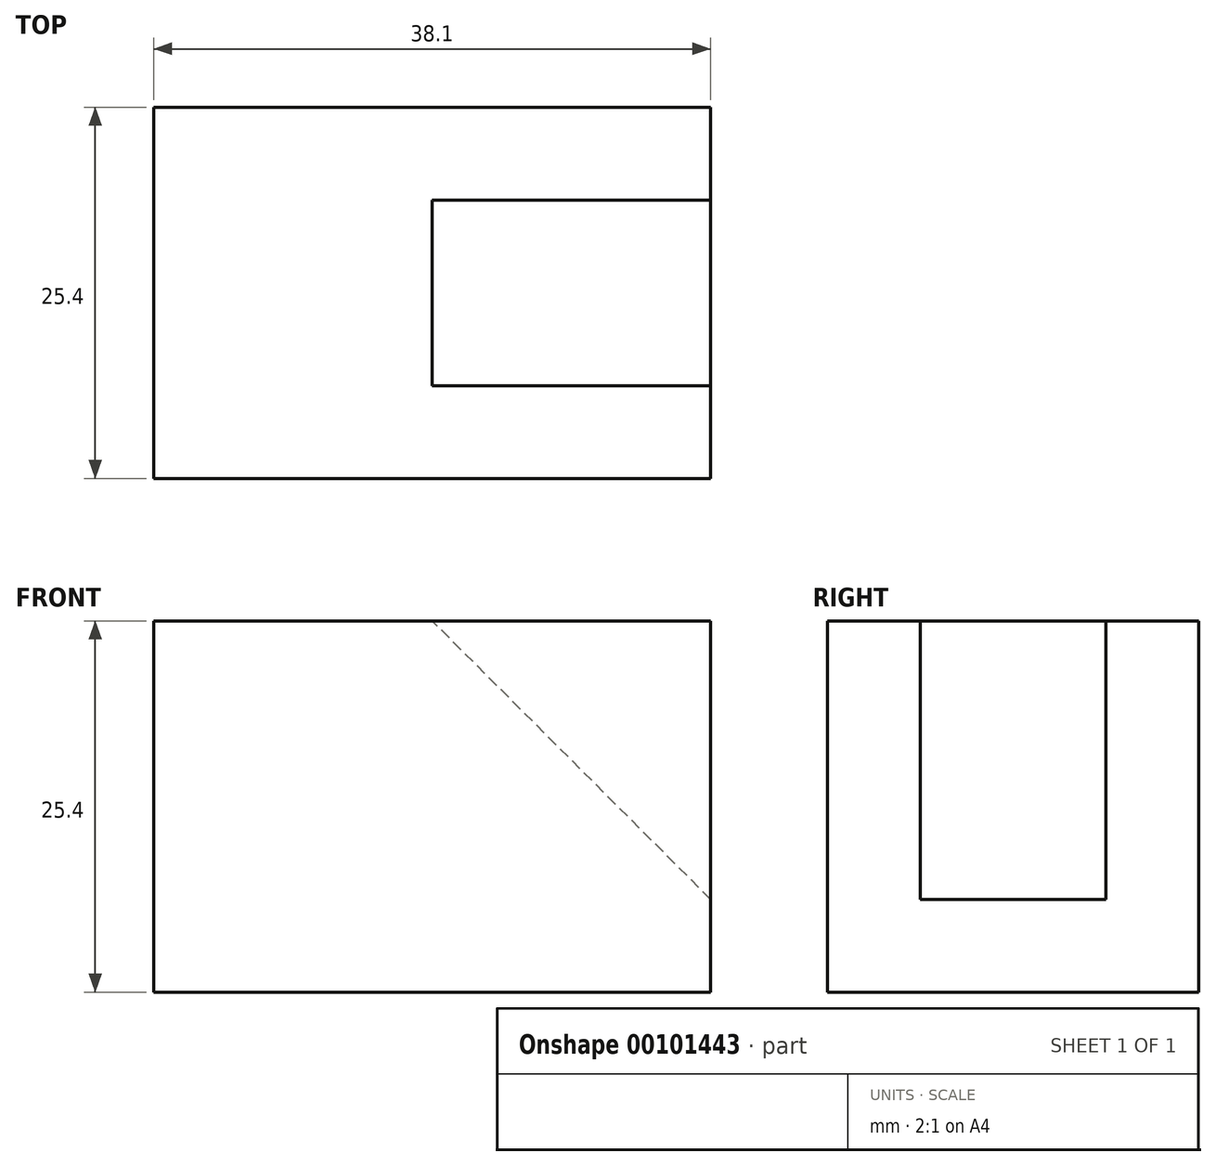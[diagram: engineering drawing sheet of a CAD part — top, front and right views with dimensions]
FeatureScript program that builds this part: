
annotation { "Feature Type Name" : "Feature", "Feature Type Description" : "" }
export const myFeature = defineFeature(function(context is Context, id is Id, definition is map)
    precondition{}
    {
        {
            var Q0;
            Q0=qCreatedBy(makeId("Front.planeOp"),FACE);
            var sketch = newSketch(context, id + "F0", { "sketchPlane" : qUnion([Q0])});
            skLineSegment(sketch, "E0", {"start": v(0, 0) * mm, "end": v(38.1, 0) * mm});
            skLineSegment(sketch, "E1", {"start": v(38.1, 0) * mm, "end": v(38.1, 25.4) * mm});
            skLineSegment(sketch, "E2", {"start": v(38.1, 25.4) * mm, "end": v(0, 25.4) * mm});
            skLineSegment(sketch, "E3", {"start": v(0, 25.4) * mm, "end": v(0, 0) * mm});
            skSolve(sketch);
        }
        {
            var Q0;
            Q0 = qSketchRegion(id + "F0", true);
            extrude(context, id + "F1", {"entities" : qUnion([Q0]), "endBound" : BoundingType.SYMMETRIC, "oppositeDirection" : true, "depth" : 25.4 * mm});
        }
        {
            var Q0;
            Q0=qCreatedBy(makeId("Front.planeOp"),FACE);
            var sketch = newSketch(context, id + "F2", { "sketchPlane" : qUnion([Q0])});
            skLineSegment(sketch, "E4", {"start": v(0, 0) * mm, "end": v(38.1, 0) * mm});
            skLineSegment(sketch, "E5", {"start": v(38.1, 0) * mm, "end": v(38.1, 25.4) * mm});
            skLineSegment(sketch, "E6", {"start": v(38.1, 25.4) * mm, "end": v(38.1, 6.35) * mm});
            skLineSegment(sketch, "E7", {"start": v(38.1, 25.4) * mm, "end": v(19.05, 25.4) * mm});
            skLineSegment(sketch, "E8", {"start": v(38.1, 6.35) * mm, "end": v(19.05, 25.4) * mm});
            skSolve(sketch);
        }
        {
            var Q0;
            Q0 = qSketchRegion(id + "F2", true);
            extrude(context, id + "F3", {"entities" : qUnion([Q0]), "operationType" : NewBodyOperationType.REMOVE, "endBound" : BoundingType.SYMMETRIC, "depth" : 12.7 * mm});
        }
    });
